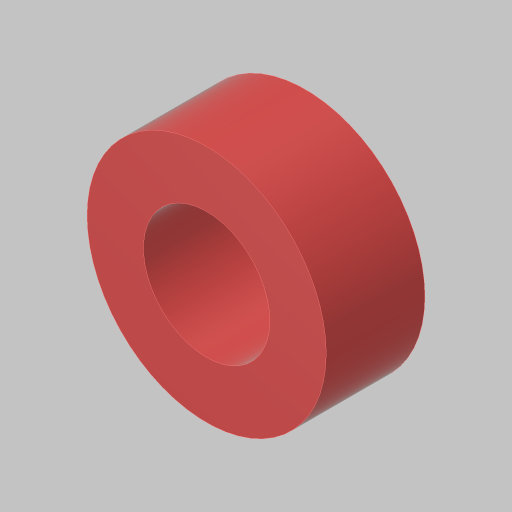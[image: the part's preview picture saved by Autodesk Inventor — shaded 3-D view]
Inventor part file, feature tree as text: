
AUTODESK INVENTOR PART (.ipt)
format: ipt  version: 2023.5 (Build 275446000, 446)  size: 107,520 bytes
history: native  units: in
note: dims shown in document units (in); Inventor stores cm internally (conversion verified against a paired STEP export)
features: extrude x1, sketch x1
ambient origin geometry x8: Origin, YZ Plane, XZ Plane, XY Plane, X Axis, Y Axis, Z Axis, Center Point
bodies: Solid1 (feature_tree)
feature tree (2):
  extrude  "Extrusion1"  Depth=0.4375in
  sketch  "Sketch1"  dims[d0=0.56in d1=0.25in d2=0.4375in d3=0.0in]
